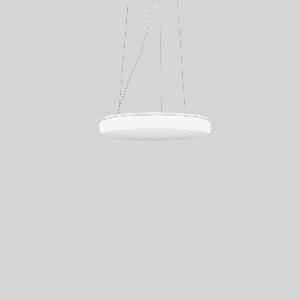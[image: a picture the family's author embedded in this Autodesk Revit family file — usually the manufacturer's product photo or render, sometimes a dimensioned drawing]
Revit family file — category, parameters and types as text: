
# Revit family: flat_polymero_kreis_slim_312241_002_1_76_9716
name_source: partatom
category: Lighting Fixtures
units: mm (PartAtom-declared; Revit-internal decimal feet)

## family parameters
Cut with Voids When Loaded = No
Host = Face
Light Source = No
Part Type = Normal
Room Calculation Point = No
Round Connector Dimension = Use Diameter
Shared = No

## types (1)
- FLAT POLYMERO KREIS SLIM (1 x LED Modul 830, 3000 lm, 3000)
    Apparent Load = 32 VA
    CIE Flux Codes = 41 72 91 83 100
    Color Rendering = 80
    Color Temperature = 3000
    Default Elevation = 1800 mm
    Description = Series: FLAT POLYMERO KREIS SLIM
Decorative round LED pendant luminaire. Base and canopy: metal, powder-coated, white. Canopy Ø 205 mm, h 35 mm. Diffuser made of non-yellowing plastic (PMMA), opal. Diffuser fastening: patented push system. Homogeneous and smooth light distribution. Suitable for pendant. 3-point steel cable suspension, steplessly adjustable. Special lengths available on request. TouchDim sensor capable. Light and/or presence sensors can be integrated. 
Colour: white
Diameter: 460 mm
Height: 68 mm
Suspension length: 200-1300 mm
Lamp: LED exchangeable
Socket: without socket
Colour temperature: 3000K
Colour rendering index (CRI): 83
System power: 32 W
Rated luminous flux: 3000 lm
Luminous efficiency: 94 lm/W
Control gear: AC power, DALI dimmable
Protection class: I
Type of protection: IP 40
    Height = 68 mm
    Lamp = 1 x LED Modul 830
    Lamp Light Flux = 3000 lm
    Lamp count = 1
    Length = 460 mm
    Lifetime = 50000 h
    Luminous efficacy = 94 lm/W
    Manufacturer = RZB
    ModVariant = No
    Model = 312241.002.1.76
    Mounting Place = Ceiling
    Mounting Type = Pendant
    Number of Poles = 1
    OnlyDefault = Yes
    Power Factor = 1
    Product Name = FLAT POLYMERO KREIS SLIM
    Product group = Pendant luminaires
    ProductGroupID = 902
    Protection Class = Protection class I
    Protection Degree = IP 40
    RLX_Detail_Level = 1
    RLX_Emergency_Light_Flux = 0 lm
    RLX_Emergency_Type = 0
    RLX_Emergency_Type_DB = No
    RlxData = <blob elided: 57809 chars, md5=8017c0e4>
    Socket = socket
    Standby Power = 0 W
    System Light Flux = 3000 lm
    System Power = 32 W
    Type Comments = Product without accessories
    Type Image = 312090.002.jpg
    URL = http://relux.com
    VarID = ---
    Voltage = 230 V
    Voltage Range = 220-240 V
    Weight = 0.00 kg
    Width = 0 mm  [stored 0 ft]

note: [stored X ft] marks values corroborated as IEEE doubles in the binary element streams (Revit-internal decimal feet)

## geometry (parser evidence)
native form markers: Blend x4, Sweep x13
no freeform markers — native parametric forms only
